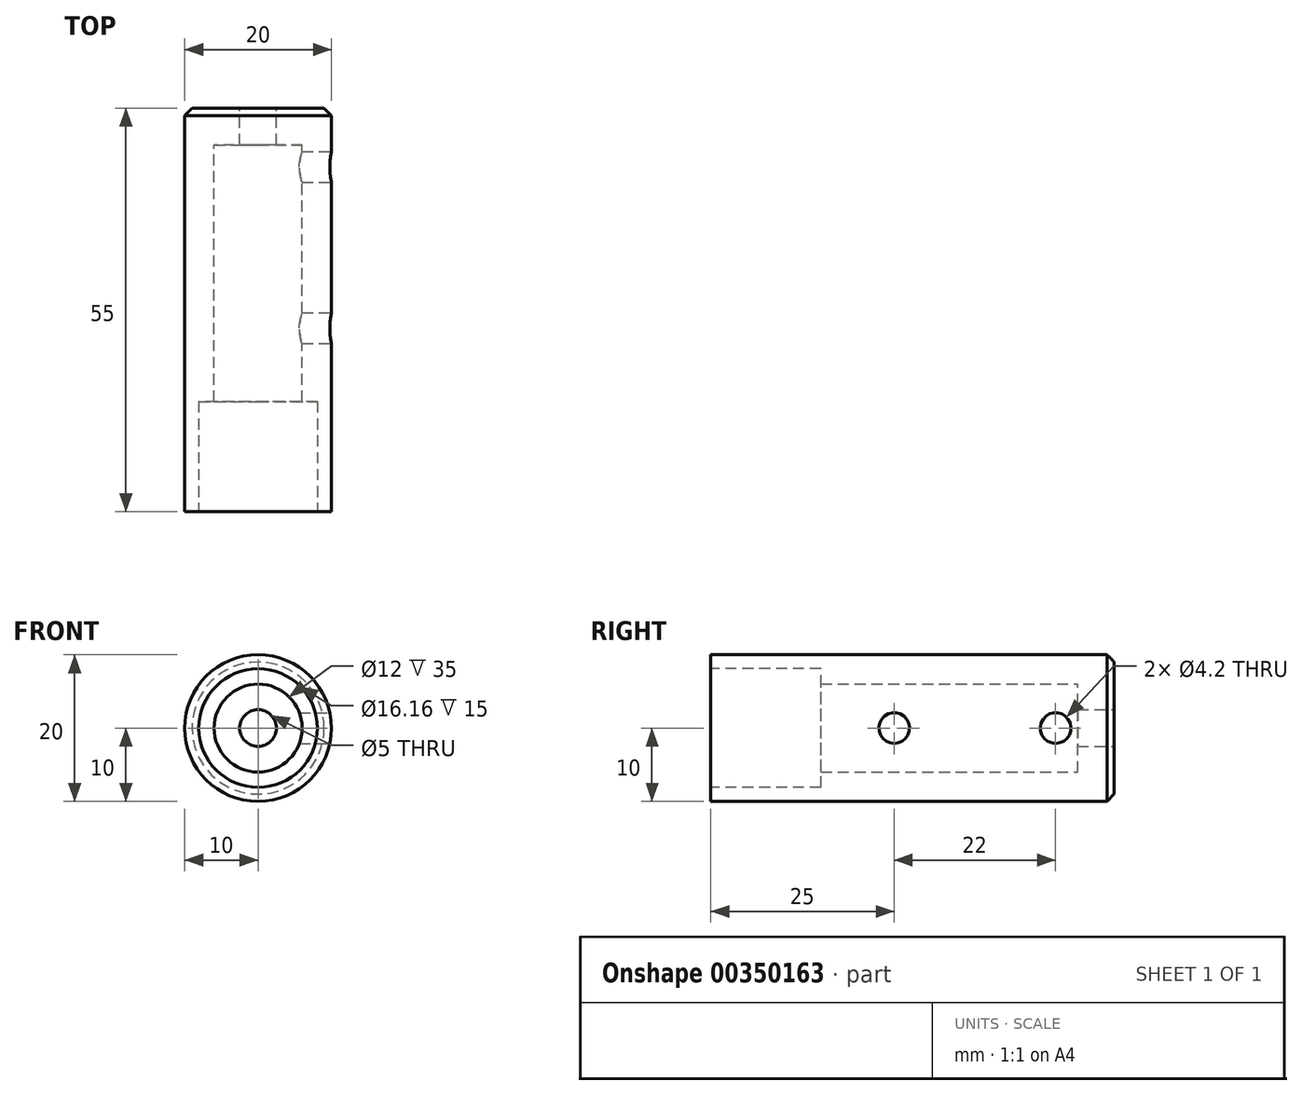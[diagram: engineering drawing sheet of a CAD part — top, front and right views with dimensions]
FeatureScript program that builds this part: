
annotation { "Feature Type Name" : "Feature", "Feature Type Description" : "" }
export const myFeature = defineFeature(function(context is Context, id is Id, definition is map)
    precondition{}
    {
        {
            var Q0;
            Q0=qCreatedBy(makeId("Front.planeOp"),FACE);
            var sketch = newSketch(context, id + "F0", { "sketchPlane" : qUnion([Q0])});
            skCircle(sketch, "E0", {"center": v(0, 0) * mm, "radius": 10 * mm});
            skCircle(sketch, "E1", {"center": v(0, 0) * mm, "radius": 6 * mm});
            skSolve(sketch);
        }
        {
            var Q0;
            Q0=makeQuery(id+"F0.imprint","IMPRINT",FACE,{"disambiguationData":[TD([[makeQuery(id+"F0.imprint","IMPRINT",EDGE,{"derivedFrom":sQuery(id+"F0.wireOp",EDGE,"E0")}),1.0]])]});
            extrude(context, id + "F1", {"entities" : qUnion([Q0]), "depth" : 50 * mm});
        }
        {
            var Q0;
            Q0=makeQuery(id+"F1.opExtrude","CAP_FACE",FACE,{"disambiguationData":[OSD([sQuery(id+"F0.wireOp",EDGE,"E0"),sQuery(id+"F0.wireOp",EDGE,"E1")])],"isStart":true});
            var sketch = newSketch(context, id + "F2", { "sketchPlane" : qUnion([Q0])});
            skCircle(sketch, "E2", {"center": v(0, 0) * mm, "radius": 10 * mm});
            skSolve(sketch);
        }
        {
            var Q0;
            Q0 = qSketchRegion(id + "F2", true);
            extrude(context, id + "F3", {"entities" : qUnion([Q0]), "operationType" : NewBodyOperationType.ADD, "depth" : 5 * mm});
        }
        {
            var Q0;
            Q0=makeQuery(id+"F1.opExtrude","CAP_FACE",FACE,{"disambiguationData":[OSD([sQuery(id+"F0.wireOp",EDGE,"E0"),sQuery(id+"F0.wireOp",EDGE,"E1")])],"isStart":false});
            var sketch = newSketch(context, id + "F4", { "sketchPlane" : qUnion([Q0])});
            skCircle(sketch, "E3", {"center": v(0, 0) * mm, "radius": 8.08 * mm});
            skSolve(sketch);
        }
        {
            var Q0;
            Q0 = qSketchRegion(id + "F4", true);
            extrude(context, id + "F5", {"entities" : qUnion([Q0]), "operationType" : NewBodyOperationType.REMOVE, "oppositeDirection" : true, "depth" : 15 * mm});
        }
        {
            var Q0;
            Q0=makeQuery(id+"F3.opExtrude","CAP_FACE",FACE,{"disambiguationData":[OSD([sQuery(id+"F2.wireOp",EDGE,"E2")])],"isStart":false});
            var sketch = newSketch(context, id + "F6", { "sketchPlane" : qUnion([Q0])});
            skCircle(sketch, "E4", {"center": v(0, 0) * mm, "radius": 2.5 * mm});
            skSolve(sketch);
        }
        {
            var Q0;
            Q0 = qSketchRegion(id + "F6", true);
            extrude(context, id + "F7", {"entities" : qUnion([Q0]), "operationType" : NewBodyOperationType.REMOVE, "endBound" : BoundingType.THROUGH_ALL, "oppositeDirection" : true, "depth" : 29.05 * mm});
        }
        {
            var Q0;
            Q0=makeQuery(id+"F3.opExtrude","CAP_EDGE",EDGE,{"disambiguationData":[OSD([sQuery(id+"F2.wireOp",EDGE,"E2")])],"isStart":false});
            chamfer(context, id + "F8", {"entities" : qUnion([Q0]), "width" : 1 * mm, "tangentPropagation" : true});
        }
        {
            var Q0;
            Q0=qCreatedBy(makeId("Right.planeOp"),FACE);
            cPlane(context, id + "F9", {"entities" : qUnion([Q0]), "cplaneType" : CPlaneType.OFFSET, "offset" : 10 * mm, "width" : 150 * mm, "height" : 150 * mm});
        }
        {
            var Q0;
            Q0=qCreatedBy(id+"F9.planeOp",FACE);
            var sketch = newSketch(context, id + "F10", { "sketchPlane" : qUnion([Q0])});
            skPoint(sketch, "E5", {"position": v(-3, 0) * mm});
            skPoint(sketch, "E6", {"position": v(-25, 0) * mm});
            skSolve(sketch);
        }
        {
            var Q0;
            Q0=sQuery(id+"F10.wireOp",VERTEX,"E6");
            var Q1;
            Q1=sQuery(id+"F10.wireOp",VERTEX,"E5");
            var Q2;
            Q2=makeQuery(id+"F1.opExtrude","SWEPT_BODY",BODY,{"disambiguationData":[OSD([sQuery(id+"F0.wireOp",EDGE,"E0"),sQuery(id+"F0.wireOp",EDGE,"E1")])]});
            hole(context, id + "F11", {"style" : HoleStyle.SIMPLE, "endStyle" : HoleEndStyle.BLIND, "standardTappedOrClearance" : lookupTablePath({ "fit" : "Normal", "standard" : "ISO", "engagement" : "75%", "pitch" : "0.8 mm", "size" : "M5", "type" : "Tapped" }), "standardBlindInLast" : lookupTablePath({ "fit" : "Standard", "standard" : "ISO", "engagement" : "75%", "pitch" : "0.8 mm", "size" : "M5", "type" : "Tapped" }), "holeDiameter" : 4.2 * mm, "showTappedDepth" : true, "holeDepth" : 7.4 * mm, "tappedDepth" : 5 * mm, "tapClearance" : 3, "locations" : qUnion([Q0, Q1]), "scope" : qUnion([Q2]), "majorDiameter" : 5 * mm});
        }
    });
